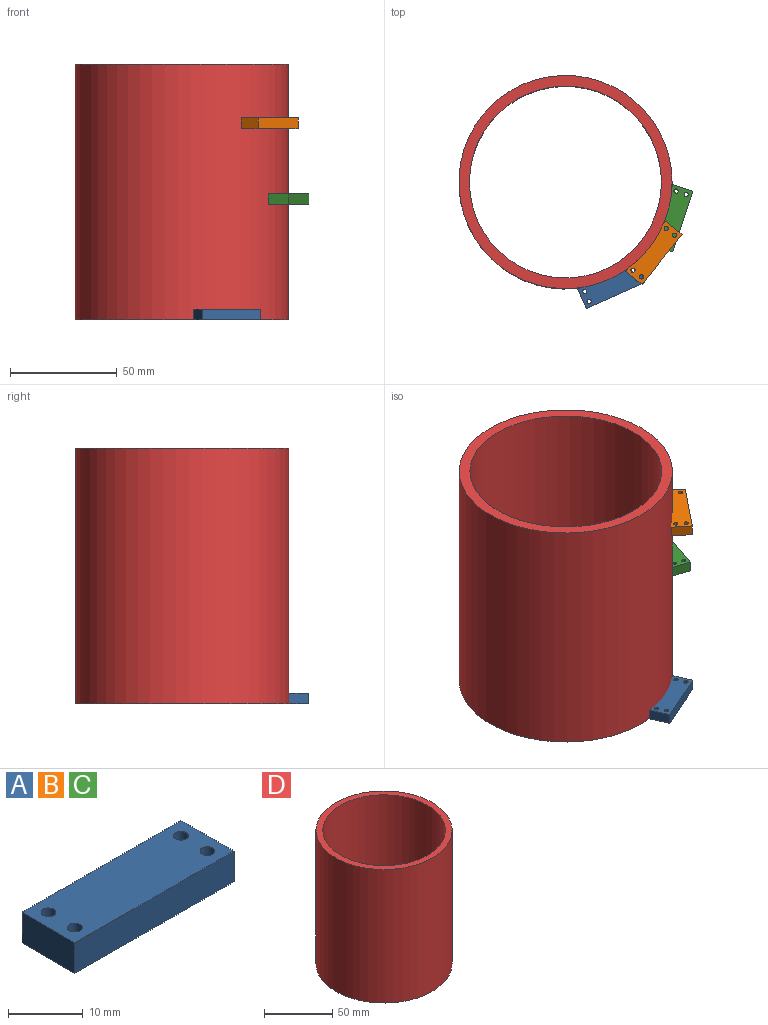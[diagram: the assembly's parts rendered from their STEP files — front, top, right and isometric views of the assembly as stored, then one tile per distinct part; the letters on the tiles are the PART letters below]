
ASSEMBLY  parts=4 mates=3
PART A: 10 faces, bbox 30x10x5 mm
  f0: plane 10x5mm, normal (1,0,0), area 50mm2, adj f1,f6,f8,f9
  f1: plane 30x5mm, normal (0,1,0), area 150mm2, adj f0,f2,f8,f9
  f2: plane 10x5mm, normal (-1,0,0), area 50mm2, adj f1,f6,f8,f9
  f3: cylinder r=1mm len=5mm, axis (0,0,-1), area 31.4mm2, adj f8,f9
  f4: cylinder r=1mm len=5mm, axis (0,0,-1), area 31.4mm2, adj f8,f9
  f5: cylinder r=1mm len=5mm, axis (0,0,-1), area 31.4mm2, adj f8,f9
  f6: plane 30x5mm, normal (0,-1,0), area 150mm2, adj f0,f2,f8,f9
  f7: cylinder r=1mm len=5mm, axis (0,0,-1), area 31.4mm2, adj f8,f9
  f8: plane 30x10mm, normal (0,0,1), area 287.4mm2, adj f0,f1,f2,f3,f4,f5,f6,f7
  f9: plane 30x10mm, normal (0,0,-1), area 287.4mm2, adj f0,f1,f2,f3,f4,f5,f6,f7
PART B: same geometry as A
PART C: same geometry as A
PART D: 4 faces, bbox 100x100x120 mm
  f0: cylinder r=45mm len=120mm, axis (0,0,-1), area 33929.2mm2, adj f2,f3
  f1: cylinder r=50mm len=120mm, axis (0,0,-1), area 37699.1mm2, adj f2,f3
  f2: plane 100x100mm, normal (0,0,1), area 1492.3mm2, adj f0,f1
  f3: plane 100x100mm, normal (0,0,-1), area 1492.3mm2, adj f0,f1
PLACE A rot(axis=(0,0,1),23.9deg) t=(0,0,0)mm
PLACE B rot(axis=(0,0,1),51.3deg) t=(0,0,89.77)mm
PLACE C rot(axis=(0,0,1),71.5deg) t=(0,0,54.14)mm
PLACE D at identity fixed
MATE cylindrical B.f9 <-> D.f0  axis (0,0,-1) through (0,0,89.77)mm
MATE cylindrical C.f9 <-> D.f1  axis (0,0,-1) through (0,0,54.14)mm
MATE revolute A.f9 <-> D.f1  axis (0,0,-1) through (0,0,0)mm
